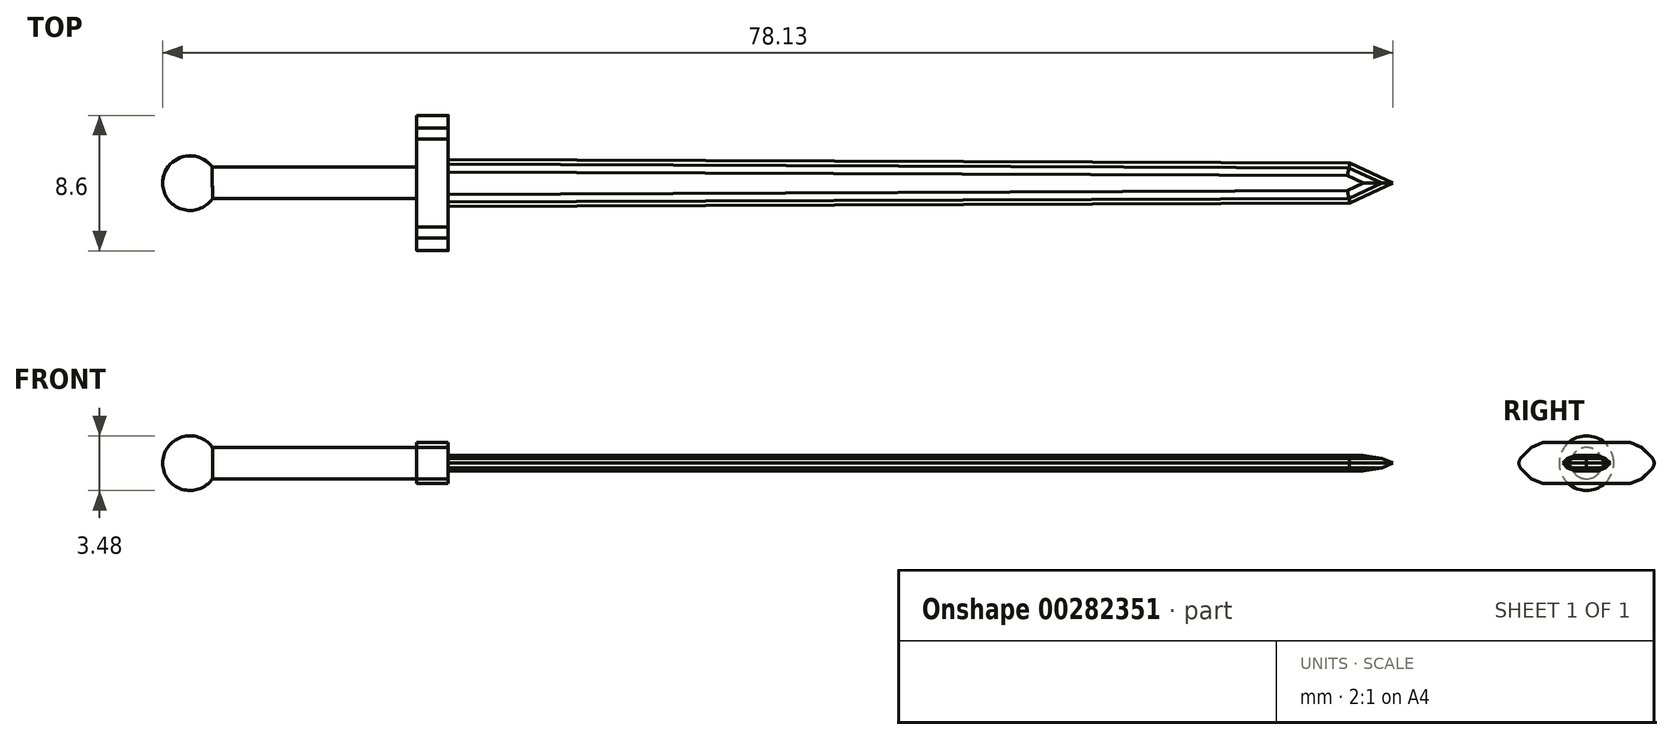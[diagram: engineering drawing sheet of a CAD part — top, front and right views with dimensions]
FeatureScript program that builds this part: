
annotation { "Feature Type Name" : "Feature", "Feature Type Description" : "" }
export const myFeature = defineFeature(function(context is Context, id is Id, definition is map)
    precondition{}
    {
        {
            var Q0;
            Q0=qCreatedBy(makeId("Top.planeOp"),FACE);
            var sketch = newSketch(context, id + "F0", { "sketchPlane" : qUnion([Q0])});
            skLineSegment(sketch, "E0", {"start": v(-22.33, -1) * mm, "end": v(-22.33, 0) * mm});
            skArc(sketch, "E1", {"start": v(-25.46, 0) * mm, "mid": v(-24.25, -1.66) * mm, "end": v(-22.3, -1) * mm});
            skLineSegment(sketch, "E2", {"start": v(-25.46, 0) * mm, "end": v(-22.33, 0) * mm});
            skLineSegment(sketch, "E3", {"start": v(-22.3, -1) * mm, "end": v(-22.33, -1) * mm});
            skSolve(sketch);
        }
        {
            var Q0;
            Q0=qCreatedBy(makeId("Top.planeOp"),FACE);
            var sketch = newSketch(context, id + "F1", { "sketchPlane" : qUnion([Q0])});
            skLineSegment(sketch, "E4", {"start": v(-9.33, -1) * mm, "end": v(-22.33, -1) * mm});
            skLineSegment(sketch, "E5", {"start": v(-22.33, 0) * mm, "end": v(-9.33, 0) * mm});
            skLineSegment(sketch, "E6", {"start": v(-22.33, -1) * mm, "end": v(-22.33, 0) * mm});
            skLineSegment(sketch, "E7", {"start": v(-9.33, -1) * mm, "end": v(-9.33, 0) * mm});
            skSolve(sketch);
        }
        {
            var Q0;
            Q0=qCreatedBy(makeId("Top.planeOp"),FACE);
            var sketch = newSketch(context, id + "F2", { "sketchPlane" : qUnion([Q0])});
            skLineSegment(sketch, "E8", {"start": v(-7.33, 0) * mm, "end": v(-7.33, 1.5) * mm});
            skLineSegment(sketch, "E9", {"start": v(-7.33, 0) * mm, "end": v(-7.33, -1.5) * mm});
            skLineSegment(sketch, "E10", {"start": v(-7.33, 1.5) * mm, "end": v(-7.32, 4.5) * mm});
            skLineSegment(sketch, "E11", {"start": v(-7.32, 4.5) * mm, "end": v(-9.32, 4.5) * mm});
            skLineSegment(sketch, "E12", {"start": v(-9.33, -4.5) * mm, "end": v(-7.33, -4.5) * mm});
            skLineSegment(sketch, "E13", {"start": v(-7.33, -4.5) * mm, "end": v(-7.33, -1.5) * mm});
            skLineSegment(sketch, "E14", {"start": v(-9.33, 1) * mm, "end": v(-9.32, 4.5) * mm});
            skLineSegment(sketch, "E15", {"start": v(-9.33, -1) * mm, "end": v(-9.33, 1) * mm});
            skLineSegment(sketch, "E16", {"start": v(-9.33, -4.5) * mm, "end": v(-9.33, -1) * mm});
            skSolve(sketch);
        }
        {
            var Q0;
            Q0=qCreatedBy(makeId("Top.planeOp"),FACE);
            var sketch = newSketch(context, id + "F3", { "sketchPlane" : qUnion([Q0])});
            skLineSegment(sketch, "E17", {"start": v(-7.33, 0) * mm, "end": v(52.67, 0) * mm});
            skLineSegment(sketch, "E18", {"start": v(52.67, 0) * mm, "end": v(49.95, -1.27) * mm});
            skLineSegment(sketch, "E19", {"start": v(52.67, 0) * mm, "end": v(49.95, 1.26) * mm});
            skLineSegment(sketch, "E20", {"start": v(-7.33, 0) * mm, "end": v(-7.33, 1.5) * mm});
            skLineSegment(sketch, "E21", {"start": v(-7.33, 0) * mm, "end": v(-7.33, -1.5) * mm});
            skLineSegment(sketch, "E22", {"start": v(-7.33, -1.5) * mm, "end": v(49.95, -1.27) * mm});
            skLineSegment(sketch, "E23", {"start": v(-7.33, 1.5) * mm, "end": v(49.95, 1.26) * mm});
            skSolve(sketch);
        }
        {
            var Q0;
            Q0=makeQuery(id+"F1.imprint","IMPRINT",FACE,{"disambiguationData":[TD([[makeQuery(id+"F1.imprint","IMPRINT",EDGE,{"derivedFrom":sQuery(id+"F1.wireOp",EDGE,"E4")}),-1.0]])]});
            var Q1;
            Q1=sQuery(id+"F1.wireOp",EDGE,"E5");
            revolve(context, id + "F4", {"entities" : qUnion([Q0]), "axis" : qUnion([Q1]), "revolveType" : RevolveType.FULL});
        }
        {
            var Q0;
            Q0 = qSketchRegion(id + "F0", true);
            var Q1;
            Q1=sQuery(id+"F0.wireOp",EDGE,"E2");
            revolve(context, id + "F5", {"operationType" : NewBodyOperationType.ADD, "entities" : qUnion([Q0]), "axis" : qUnion([Q1]), "revolveType" : RevolveType.FULL});
        }
        {
            var Q0;
            Q0 = qSketchRegion(id + "F2", true);
            extrude(context, id + "F6", {"entities" : qUnion([Q0]), "operationType" : NewBodyOperationType.ADD, "oppositeDirection" : true, "depth" : 1.3 * mm, "hasSecondDirection" : true, "secondDirectionOppositeDirection" : false, "secondDirectionDepth" : 1.3 * mm});
        }
        {
            var Q0;
            Q0=makeQuery(id+"F3.imprint","IMPRINT",FACE,{"disambiguationData":[TD([[makeQuery(id+"F3.imprint","IMPRINT",EDGE,{"derivedFrom":sQuery(id+"F3.wireOp",EDGE,"E17")}),1.0]])]});
            var Q1;
            Q1=makeQuery(id+"F3.imprint","IMPRINT",FACE,{"disambiguationData":[TD([[makeQuery(id+"F3.imprint","IMPRINT",EDGE,{"derivedFrom":sQuery(id+"F3.wireOp",EDGE,"E17")}),-1.0]])]});
            extrude(context, id + "F7", {"entities" : qUnion([Q0, Q1]), "operationType" : NewBodyOperationType.ADD, "depth" : 0.5 * mm, "hasSecondDirection" : true, "secondDirectionOppositeDirection" : true, "secondDirectionDepth" : 0.5 * mm});
        }
        {
            var Q0;
            Q0=makeQuery(id+"F7.opExtrude","CAP_EDGE",EDGE,{"disambiguationData":[OSD([sQuery(id+"F3.wireOp",EDGE,"E22")])],"isStart":false});
            var Q1;
            Q1=makeQuery(id+"F7.opExtrude","CAP_EDGE",EDGE,{"disambiguationData":[OSD([sQuery(id+"F3.wireOp",EDGE,"E22")])],"isStart":true});
            var Q2;
            Q2=makeQuery(id+"F7.opExtrude","CAP_EDGE",EDGE,{"disambiguationData":[OSD([sQuery(id+"F3.wireOp",EDGE,"E23")])],"isStart":false});
            var Q3;
            Q3=makeQuery(id+"F7.opExtrude","CAP_EDGE",EDGE,{"disambiguationData":[OSD([sQuery(id+"F3.wireOp",EDGE,"E23")])],"isStart":true});
            var Q4;
            Q4=makeQuery(id+"F7.opExtrude","CAP_EDGE",EDGE,{"disambiguationData":[OSD([sQuery(id+"F3.wireOp",EDGE,"E18")])],"isStart":false});
            var Q5;
            Q5=makeQuery(id+"F7.opExtrude","CAP_EDGE",EDGE,{"disambiguationData":[OSD([sQuery(id+"F3.wireOp",EDGE,"E19")])],"isStart":false});
            var Q6;
            Q6=makeQuery(id+"F7.opExtrude","CAP_EDGE",EDGE,{"disambiguationData":[OSD([sQuery(id+"F3.wireOp",EDGE,"E18")])],"isStart":true});
            var Q7;
            Q7=makeQuery(id+"F7.opExtrude","CAP_EDGE",EDGE,{"disambiguationData":[OSD([sQuery(id+"F3.wireOp",EDGE,"E19")])],"isStart":true});
            chamfer(context, id + "F8", {"entities" : qUnion([Q0, Q1, Q2, Q3, Q4, Q5, Q6, Q7]), "width" : 0.5 * mm, "tangentPropagation" : true});
        }
        {
            var Q0;
            Q0=makeQuery(id+"F6.opExtrude","CAP_EDGE",EDGE,{"disambiguationData":[OSD([sQuery(id+"F2.wireOp",EDGE,"E12")])],"isStart":true});
            var Q1;
            Q1=makeQuery(id+"F6.opExtrude","CAP_EDGE",EDGE,{"disambiguationData":[OSD([sQuery(id+"F2.wireOp",EDGE,"E12")])],"isStart":false});
            var Q2;
            Q2=makeQuery(id+"F6.opExtrude","CAP_EDGE",EDGE,{"disambiguationData":[OSD([sQuery(id+"F2.wireOp",EDGE,"E11")])],"isStart":true});
            var Q3;
            Q3=makeQuery(id+"F6.opExtrude","CAP_EDGE",EDGE,{"disambiguationData":[OSD([sQuery(id+"F2.wireOp",EDGE,"E11")])],"isStart":false});
            chamfer(context, id + "F9", {"entities" : qUnion([Q0, Q1, Q2, Q3]), "width" : 1.3 * mm, "tangentPropagation" : true});
        }
        {
            var Q0;
            {var subQ0=sQuery(id+"F2.wireOp",EDGE,"E12");Q0=makeQuery(id+"F9.opChamfer","BLEND_EDGE",EDGE,{"blendedFrom":[makeQuery(id+"F6.opExtrude","CAP_EDGE",EDGE,{"disambiguationData":[OSD([subQ0])],"isStart":true}),makeQuery(id+"F6.opExtrude","CAP_FACE",FACE,{"disambiguationData":[OSD([sQuery(id+"F2.wireOp",EDGE,"E8"),sQuery(id+"F2.wireOp",EDGE,"E9"),sQuery(id+"F2.wireOp",EDGE,"E10"),sQuery(id+"F2.wireOp",EDGE,"E11"),subQ0,sQuery(id+"F2.wireOp",EDGE,"E13"),sQuery(id+"F2.wireOp",EDGE,"E14"),sQuery(id+"F2.wireOp",EDGE,"E15"),sQuery(id+"F2.wireOp",EDGE,"E16")])],"isStart":true})],"blendedInto":[makeQuery(id+"F6.opExtrude","CAP_FACE",FACE,{"disambiguationData":[OSD([sQuery(id+"F2.wireOp",EDGE,"E8"),sQuery(id+"F2.wireOp",EDGE,"E9"),sQuery(id+"F2.wireOp",EDGE,"E10"),sQuery(id+"F2.wireOp",EDGE,"E11"),subQ0,sQuery(id+"F2.wireOp",EDGE,"E13"),sQuery(id+"F2.wireOp",EDGE,"E14"),sQuery(id+"F2.wireOp",EDGE,"E15"),sQuery(id+"F2.wireOp",EDGE,"E16")])],"isStart":true})]});}
            var Q1;
            {var subQ0=sQuery(id+"F2.wireOp",EDGE,"E11");Q1=makeQuery(id+"F9.opChamfer","BLEND_EDGE",EDGE,{"blendedFrom":[makeQuery(id+"F6.opExtrude","CAP_EDGE",EDGE,{"disambiguationData":[OSD([subQ0])],"isStart":true}),makeQuery(id+"F6.opExtrude","CAP_FACE",FACE,{"disambiguationData":[OSD([sQuery(id+"F2.wireOp",EDGE,"E8"),sQuery(id+"F2.wireOp",EDGE,"E9"),sQuery(id+"F2.wireOp",EDGE,"E10"),subQ0,sQuery(id+"F2.wireOp",EDGE,"E12"),sQuery(id+"F2.wireOp",EDGE,"E13"),sQuery(id+"F2.wireOp",EDGE,"E14"),sQuery(id+"F2.wireOp",EDGE,"E15"),sQuery(id+"F2.wireOp",EDGE,"E16")])],"isStart":true})],"blendedInto":[makeQuery(id+"F6.opExtrude","CAP_FACE",FACE,{"disambiguationData":[OSD([sQuery(id+"F2.wireOp",EDGE,"E8"),sQuery(id+"F2.wireOp",EDGE,"E9"),sQuery(id+"F2.wireOp",EDGE,"E10"),subQ0,sQuery(id+"F2.wireOp",EDGE,"E12"),sQuery(id+"F2.wireOp",EDGE,"E13"),sQuery(id+"F2.wireOp",EDGE,"E14"),sQuery(id+"F2.wireOp",EDGE,"E15"),sQuery(id+"F2.wireOp",EDGE,"E16")])],"isStart":true})]});}
            var Q2;
            {var subQ0=sQuery(id+"F2.wireOp",EDGE,"E11");Q2=makeQuery(id+"F9.opChamfer","BLEND_EDGE",EDGE,{"blendedFrom":[makeQuery(id+"F6.opExtrude","CAP_EDGE",EDGE,{"disambiguationData":[OSD([subQ0])],"isStart":false}),makeQuery(id+"F6.opExtrude","CAP_FACE",FACE,{"disambiguationData":[OSD([sQuery(id+"F2.wireOp",EDGE,"E8"),sQuery(id+"F2.wireOp",EDGE,"E9"),sQuery(id+"F2.wireOp",EDGE,"E10"),subQ0,sQuery(id+"F2.wireOp",EDGE,"E12"),sQuery(id+"F2.wireOp",EDGE,"E13"),sQuery(id+"F2.wireOp",EDGE,"E14"),sQuery(id+"F2.wireOp",EDGE,"E15"),sQuery(id+"F2.wireOp",EDGE,"E16")])],"isStart":false})],"blendedInto":[makeQuery(id+"F6.opExtrude","CAP_FACE",FACE,{"disambiguationData":[OSD([sQuery(id+"F2.wireOp",EDGE,"E8"),sQuery(id+"F2.wireOp",EDGE,"E9"),sQuery(id+"F2.wireOp",EDGE,"E10"),subQ0,sQuery(id+"F2.wireOp",EDGE,"E12"),sQuery(id+"F2.wireOp",EDGE,"E13"),sQuery(id+"F2.wireOp",EDGE,"E14"),sQuery(id+"F2.wireOp",EDGE,"E15"),sQuery(id+"F2.wireOp",EDGE,"E16")])],"isStart":false})]});}
            var Q3;
            {var subQ0=sQuery(id+"F2.wireOp",EDGE,"E12");Q3=makeQuery(id+"F9.opChamfer","BLEND_EDGE",EDGE,{"blendedFrom":[makeQuery(id+"F6.opExtrude","CAP_EDGE",EDGE,{"disambiguationData":[OSD([subQ0])],"isStart":false}),makeQuery(id+"F6.opExtrude","CAP_FACE",FACE,{"disambiguationData":[OSD([sQuery(id+"F2.wireOp",EDGE,"E8"),sQuery(id+"F2.wireOp",EDGE,"E9"),sQuery(id+"F2.wireOp",EDGE,"E10"),sQuery(id+"F2.wireOp",EDGE,"E11"),subQ0,sQuery(id+"F2.wireOp",EDGE,"E13"),sQuery(id+"F2.wireOp",EDGE,"E14"),sQuery(id+"F2.wireOp",EDGE,"E15"),sQuery(id+"F2.wireOp",EDGE,"E16")])],"isStart":false})],"blendedInto":[makeQuery(id+"F6.opExtrude","CAP_FACE",FACE,{"disambiguationData":[OSD([sQuery(id+"F2.wireOp",EDGE,"E8"),sQuery(id+"F2.wireOp",EDGE,"E9"),sQuery(id+"F2.wireOp",EDGE,"E10"),sQuery(id+"F2.wireOp",EDGE,"E11"),subQ0,sQuery(id+"F2.wireOp",EDGE,"E13"),sQuery(id+"F2.wireOp",EDGE,"E14"),sQuery(id+"F2.wireOp",EDGE,"E15"),sQuery(id+"F2.wireOp",EDGE,"E16")])],"isStart":false})]});}
            chamfer(context, id + "F10", {"entities" : qUnion([Q0, Q1, Q2, Q3]), "width" : 1 * mm, "tangentPropagation" : true});
        }
        {
            var Q0;
            {var subQ0=sQuery(id+"F2.wireOp",EDGE,"E12");Q0=makeQuery(id+"F9.opChamfer","BLEND_EDGE",EDGE,{"blendedFrom":[makeQuery(id+"F6.opExtrude","CAP_EDGE",EDGE,{"disambiguationData":[OSD([subQ0])],"isStart":true}),makeQuery(id+"F6.opExtrude","CAP_EDGE",EDGE,{"disambiguationData":[OSD([subQ0])],"isStart":false})],"blendedInto":[]});}
            var Q1;
            {var subQ0=sQuery(id+"F2.wireOp",EDGE,"E11");Q1=makeQuery(id+"F9.opChamfer","BLEND_EDGE",EDGE,{"blendedFrom":[makeQuery(id+"F6.opExtrude","CAP_EDGE",EDGE,{"disambiguationData":[OSD([subQ0])],"isStart":true}),makeQuery(id+"F6.opExtrude","CAP_EDGE",EDGE,{"disambiguationData":[OSD([subQ0])],"isStart":false})],"blendedInto":[]});}
            fillet(context, id + "F11", {"entities" : qUnion([Q0, Q1]), "radius" : 0.5 * mm, "tangentPropagation" : true, "allowEdgeOverflow" : false});
        }
        {
            var Q0;
            {var subQ0=sQuery(id+"F3.wireOp",EDGE,"E18");Q0=makeQuery(id+"F8.opChamfer","BLEND_EDGE",EDGE,{"blendedFrom":[makeQuery(id+"F7.opExtrude","CAP_EDGE",EDGE,{"disambiguationData":[OSD([subQ0])],"isStart":false}),makeQuery(id+"F7.opExtrude","CAP_FACE",FACE,{"disambiguationData":[OSD([subQ0,sQuery(id+"F3.wireOp",EDGE,"E19"),sQuery(id+"F3.wireOp",EDGE,"E20"),sQuery(id+"F3.wireOp",EDGE,"E21"),sQuery(id+"F3.wireOp",EDGE,"E22"),sQuery(id+"F3.wireOp",EDGE,"E23")])],"isStart":false})],"blendedInto":[makeQuery(id+"F7.opExtrude","CAP_FACE",FACE,{"disambiguationData":[OSD([subQ0,sQuery(id+"F3.wireOp",EDGE,"E19"),sQuery(id+"F3.wireOp",EDGE,"E20"),sQuery(id+"F3.wireOp",EDGE,"E21"),sQuery(id+"F3.wireOp",EDGE,"E22"),sQuery(id+"F3.wireOp",EDGE,"E23")])],"isStart":false})]});}
            var Q1;
            {var subQ0=sQuery(id+"F3.wireOp",EDGE,"E22");Q1=makeQuery(id+"F8.opChamfer","BLEND_EDGE",EDGE,{"blendedFrom":[makeQuery(id+"F7.opExtrude","CAP_EDGE",EDGE,{"disambiguationData":[OSD([subQ0])],"isStart":false}),makeQuery(id+"F7.opExtrude","CAP_FACE",FACE,{"disambiguationData":[OSD([sQuery(id+"F3.wireOp",EDGE,"E18"),sQuery(id+"F3.wireOp",EDGE,"E19"),sQuery(id+"F3.wireOp",EDGE,"E20"),sQuery(id+"F3.wireOp",EDGE,"E21"),subQ0,sQuery(id+"F3.wireOp",EDGE,"E23")])],"isStart":false})],"blendedInto":[makeQuery(id+"F7.opExtrude","CAP_FACE",FACE,{"disambiguationData":[OSD([sQuery(id+"F3.wireOp",EDGE,"E18"),sQuery(id+"F3.wireOp",EDGE,"E19"),sQuery(id+"F3.wireOp",EDGE,"E20"),sQuery(id+"F3.wireOp",EDGE,"E21"),subQ0,sQuery(id+"F3.wireOp",EDGE,"E23")])],"isStart":false})]});}
            var Q2;
            {var subQ0=sQuery(id+"F3.wireOp",EDGE,"E23");Q2=makeQuery(id+"F8.opChamfer","BLEND_EDGE",EDGE,{"blendedFrom":[makeQuery(id+"F7.opExtrude","CAP_EDGE",EDGE,{"disambiguationData":[OSD([subQ0])],"isStart":false}),makeQuery(id+"F7.opExtrude","CAP_FACE",FACE,{"disambiguationData":[OSD([sQuery(id+"F3.wireOp",EDGE,"E18"),sQuery(id+"F3.wireOp",EDGE,"E19"),sQuery(id+"F3.wireOp",EDGE,"E20"),sQuery(id+"F3.wireOp",EDGE,"E21"),sQuery(id+"F3.wireOp",EDGE,"E22"),subQ0])],"isStart":false})],"blendedInto":[makeQuery(id+"F7.opExtrude","CAP_FACE",FACE,{"disambiguationData":[OSD([sQuery(id+"F3.wireOp",EDGE,"E18"),sQuery(id+"F3.wireOp",EDGE,"E19"),sQuery(id+"F3.wireOp",EDGE,"E20"),sQuery(id+"F3.wireOp",EDGE,"E21"),sQuery(id+"F3.wireOp",EDGE,"E22"),subQ0])],"isStart":false})]});}
            var Q3;
            {var subQ0=sQuery(id+"F3.wireOp",EDGE,"E19");Q3=makeQuery(id+"F8.opChamfer","BLEND_EDGE",EDGE,{"blendedFrom":[makeQuery(id+"F7.opExtrude","CAP_EDGE",EDGE,{"disambiguationData":[OSD([subQ0])],"isStart":false}),makeQuery(id+"F7.opExtrude","CAP_FACE",FACE,{"disambiguationData":[OSD([sQuery(id+"F3.wireOp",EDGE,"E18"),subQ0,sQuery(id+"F3.wireOp",EDGE,"E20"),sQuery(id+"F3.wireOp",EDGE,"E21"),sQuery(id+"F3.wireOp",EDGE,"E22"),sQuery(id+"F3.wireOp",EDGE,"E23")])],"isStart":false})],"blendedInto":[makeQuery(id+"F7.opExtrude","CAP_FACE",FACE,{"disambiguationData":[OSD([sQuery(id+"F3.wireOp",EDGE,"E18"),subQ0,sQuery(id+"F3.wireOp",EDGE,"E20"),sQuery(id+"F3.wireOp",EDGE,"E21"),sQuery(id+"F3.wireOp",EDGE,"E22"),sQuery(id+"F3.wireOp",EDGE,"E23")])],"isStart":false})]});}
            var Q4;
            {var subQ0=sQuery(id+"F3.wireOp",EDGE,"E23");Q4=makeQuery(id+"F8.opChamfer","BLEND_EDGE",EDGE,{"blendedFrom":[makeQuery(id+"F7.opExtrude","CAP_EDGE",EDGE,{"disambiguationData":[OSD([subQ0])],"isStart":true}),makeQuery(id+"F7.opExtrude","CAP_FACE",FACE,{"disambiguationData":[OSD([sQuery(id+"F3.wireOp",EDGE,"E18"),sQuery(id+"F3.wireOp",EDGE,"E19"),sQuery(id+"F3.wireOp",EDGE,"E20"),sQuery(id+"F3.wireOp",EDGE,"E21"),sQuery(id+"F3.wireOp",EDGE,"E22"),subQ0])],"isStart":true})],"blendedInto":[makeQuery(id+"F7.opExtrude","CAP_FACE",FACE,{"disambiguationData":[OSD([sQuery(id+"F3.wireOp",EDGE,"E18"),sQuery(id+"F3.wireOp",EDGE,"E19"),sQuery(id+"F3.wireOp",EDGE,"E20"),sQuery(id+"F3.wireOp",EDGE,"E21"),sQuery(id+"F3.wireOp",EDGE,"E22"),subQ0])],"isStart":true})]});}
            var Q5;
            {var subQ0=sQuery(id+"F3.wireOp",EDGE,"E22");Q5=makeQuery(id+"F8.opChamfer","BLEND_EDGE",EDGE,{"blendedFrom":[makeQuery(id+"F7.opExtrude","CAP_EDGE",EDGE,{"disambiguationData":[OSD([subQ0])],"isStart":true}),makeQuery(id+"F7.opExtrude","CAP_FACE",FACE,{"disambiguationData":[OSD([sQuery(id+"F3.wireOp",EDGE,"E18"),sQuery(id+"F3.wireOp",EDGE,"E19"),sQuery(id+"F3.wireOp",EDGE,"E20"),sQuery(id+"F3.wireOp",EDGE,"E21"),subQ0,sQuery(id+"F3.wireOp",EDGE,"E23")])],"isStart":true})],"blendedInto":[makeQuery(id+"F7.opExtrude","CAP_FACE",FACE,{"disambiguationData":[OSD([sQuery(id+"F3.wireOp",EDGE,"E18"),sQuery(id+"F3.wireOp",EDGE,"E19"),sQuery(id+"F3.wireOp",EDGE,"E20"),sQuery(id+"F3.wireOp",EDGE,"E21"),subQ0,sQuery(id+"F3.wireOp",EDGE,"E23")])],"isStart":true})]});}
            var Q6;
            {var subQ0=sQuery(id+"F3.wireOp",EDGE,"E18");Q6=makeQuery(id+"F8.opChamfer","BLEND_EDGE",EDGE,{"blendedFrom":[makeQuery(id+"F7.opExtrude","CAP_EDGE",EDGE,{"disambiguationData":[OSD([subQ0])],"isStart":true}),makeQuery(id+"F7.opExtrude","CAP_FACE",FACE,{"disambiguationData":[OSD([subQ0,sQuery(id+"F3.wireOp",EDGE,"E19"),sQuery(id+"F3.wireOp",EDGE,"E20"),sQuery(id+"F3.wireOp",EDGE,"E21"),sQuery(id+"F3.wireOp",EDGE,"E22"),sQuery(id+"F3.wireOp",EDGE,"E23")])],"isStart":true})],"blendedInto":[makeQuery(id+"F7.opExtrude","CAP_FACE",FACE,{"disambiguationData":[OSD([subQ0,sQuery(id+"F3.wireOp",EDGE,"E19"),sQuery(id+"F3.wireOp",EDGE,"E20"),sQuery(id+"F3.wireOp",EDGE,"E21"),sQuery(id+"F3.wireOp",EDGE,"E22"),sQuery(id+"F3.wireOp",EDGE,"E23")])],"isStart":true})]});}
            var Q7;
            {var subQ0=sQuery(id+"F3.wireOp",EDGE,"E19");Q7=makeQuery(id+"F8.opChamfer","BLEND_EDGE",EDGE,{"blendedFrom":[makeQuery(id+"F7.opExtrude","CAP_EDGE",EDGE,{"disambiguationData":[OSD([subQ0])],"isStart":true}),makeQuery(id+"F7.opExtrude","CAP_FACE",FACE,{"disambiguationData":[OSD([sQuery(id+"F3.wireOp",EDGE,"E18"),subQ0,sQuery(id+"F3.wireOp",EDGE,"E20"),sQuery(id+"F3.wireOp",EDGE,"E21"),sQuery(id+"F3.wireOp",EDGE,"E22"),sQuery(id+"F3.wireOp",EDGE,"E23")])],"isStart":true})],"blendedInto":[makeQuery(id+"F7.opExtrude","CAP_FACE",FACE,{"disambiguationData":[OSD([sQuery(id+"F3.wireOp",EDGE,"E18"),subQ0,sQuery(id+"F3.wireOp",EDGE,"E20"),sQuery(id+"F3.wireOp",EDGE,"E21"),sQuery(id+"F3.wireOp",EDGE,"E22"),sQuery(id+"F3.wireOp",EDGE,"E23")])],"isStart":true})]});}
            chamfer(context, id + "F12", {"entities" : qUnion([Q0, Q1, Q2, Q3, Q4, Q5, Q6, Q7]), "width" : 0.7 * mm, "tangentPropagation" : true});
        }
    });
